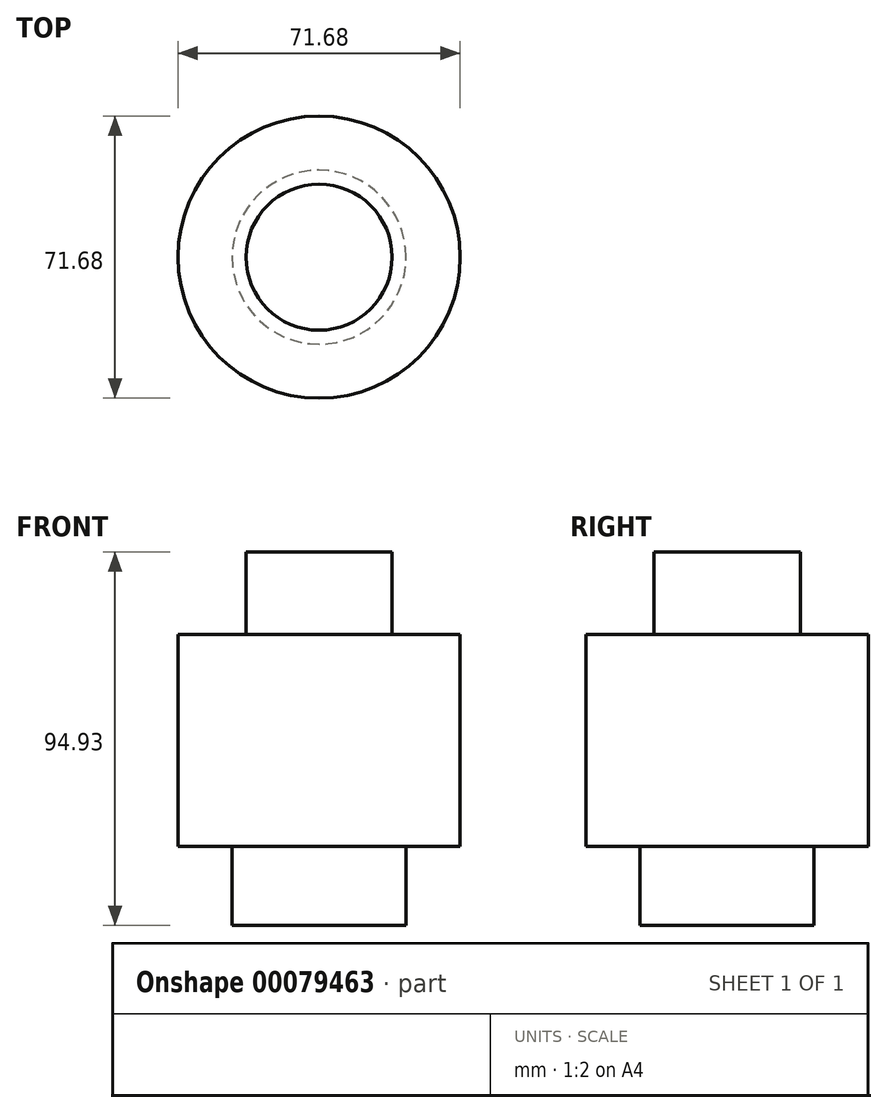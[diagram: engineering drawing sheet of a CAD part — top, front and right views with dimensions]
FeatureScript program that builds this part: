
annotation { "Feature Type Name" : "Feature", "Feature Type Description" : "" }
export const myFeature = defineFeature(function(context is Context, id is Id, definition is map)
    precondition{}
    {
        {
            var Q0;
            Q0=qCreatedBy(makeId("Top.planeOp"),FACE);
            var sketch = newSketch(context, id + "F0", { "sketchPlane" : qUnion([Q0])});
            skCircle(sketch, "E0", {"center": v(0, 0) * mm, "radius": 18.55 * mm});
            skSolve(sketch);
        }
        {
            var Q0;
            Q0=makeQuery(id+"F0.imprint","IMPRINT",FACE,{"disambiguationData":[TD([[makeQuery(id+"F0.imprint","IMPRINT",EDGE,{"derivedFrom":sQuery(id+"F0.wireOp",EDGE,"E0")}),1.0]])]});
            extrude(context, id + "F1", {"entities" : qUnion([Q0]), "depth" : 20.97 * mm});
        }
        {
            var Q0;
            Q0=qCreatedBy(makeId("Top.planeOp"),FACE);
            var sketch = newSketch(context, id + "F2", { "sketchPlane" : qUnion([Q0])});
            skCircle(sketch, "E1", {"center": v(0, 0) * mm, "radius": 35.84 * mm});
            skSolve(sketch);
        }
        {
            var Q0;
            Q0 = qSketchRegion(id + "F2", true);
            extrude(context, id + "F3", {"entities" : qUnion([Q0]), "operationType" : NewBodyOperationType.ADD, "oppositeDirection" : true, "depth" : 53.83 * mm});
        }
        {
            var Q0;
            Q0=makeQuery(id+"F3.opExtrude","CAP_FACE",FACE,{"disambiguationData":[OSD([sQuery(id+"F2.wireOp",EDGE,"E1")])],"isStart":false});
            var sketch = newSketch(context, id + "F4", { "sketchPlane" : qUnion([Q0])});
            skSolve(sketch);
        }
        {
            var Q0;
            Q0=makeQuery(id+"F4.imprint","IMPRINT",FACE,{"disambiguationData":[TD([[makeQuery(id+"F4.imprint","IMPRINT",EDGE,{"derivedFrom":makeQuery(id+"F3.opExtrude","CAP_EDGE",EDGE,{"disambiguationData":[OSD([sQuery(id+"F2.wireOp",EDGE,"E1")])],"isStart":false})}),-1.0]])]});
            var sketch = newSketch(context, id + "F5", { "sketchPlane" : qUnion([Q0])});
            skCircle(sketch, "E2", {"center": v(0, 0) * mm, "radius": 22.1 * mm});
            skSolve(sketch);
        }
        {
            var Q0;
            Q0 = qSketchRegion(id + "F5", true);
            extrude(context, id + "F6", {"entities" : qUnion([Q0]), "operationType" : NewBodyOperationType.ADD, "depth" : 20.13 * mm});
        }
    });
